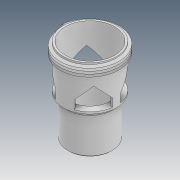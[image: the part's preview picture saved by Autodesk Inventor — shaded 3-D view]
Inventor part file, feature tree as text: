
AUTODESK INVENTOR PART (.ipt)
format: ipt  version: 2020 (Build 240168000, 168)  size: 302,592 bytes
history: native  units: mm
features: sketch x5, chamfer x4, extrude x3, revolve x1, plane x1, helix x1
ambient origin geometry x8: Origin, YZ Plane, XZ Plane, XY Plane, X Axis, Y Axis, Z Axis, Center Point
bodies: Solid1 (feature_tree)
feature tree (15):
  revolve  "Revolution1"  [1 undecoded]
  chamfer  "Chamfer1"  Distance=0.6mm Angle=45.0deg
  extrude  "Extrusion1"  Depth=26.4mm
  chamfer  "Chamfer2"  Distance=1.0mm
  extrude  "Extrusion2"  Depth=2.0mm TaperAngle=45.0deg
  extrude  "Extrusion3"  Depth=24.5mm
  chamfer  "Chamfer3"  Distance=9.0mm
  sketch  "Sketch5"  dims[d9=9.8mm d10=26.4mm d11=1.0mm d12=0.0mm d13=2.0mm d14=2.0mm d15=45.0deg d16=24.5mm d17=9.0mm d18=4.0mm d19=11.0mm d20=0.0mm d21=10.0mm d22=0.0mm d23=6.73mm d24=2.0mm d25=45.0deg d27=1.25mm d36=-0.625mm d55=1.4mm d56=1.25mm d57=5.0mm d58=10.0mm d59=0.0mm d60=90.0deg d61=90.0deg d62=0.0mm d63=0.0mm d64=0.559mm d65=2.0mm d66=45.0deg]
  plane  "Work Plane1"
  helix  "Coil3"  [1 undecoded]
  chamfer  "Chamfer5"  Distance=11.0mm
  sketch  "Sketch1"  dims[d0=20.0mm d1=11.2mm]
  sketch  "Sketch2"  dims[d2=11.0mm]
  sketch  "Sketch3"  dims[d4=180.0deg]
  sketch  "Sketch4"  dims[d5=90.0deg d6=0.6mm d7=2.0mm d8=45.0deg]
note: 2 required parameter values undecoded (feature->parameter linkage not recoverable at this tier; creation-order binding heuristic only, values carry confidence <= 0.55)